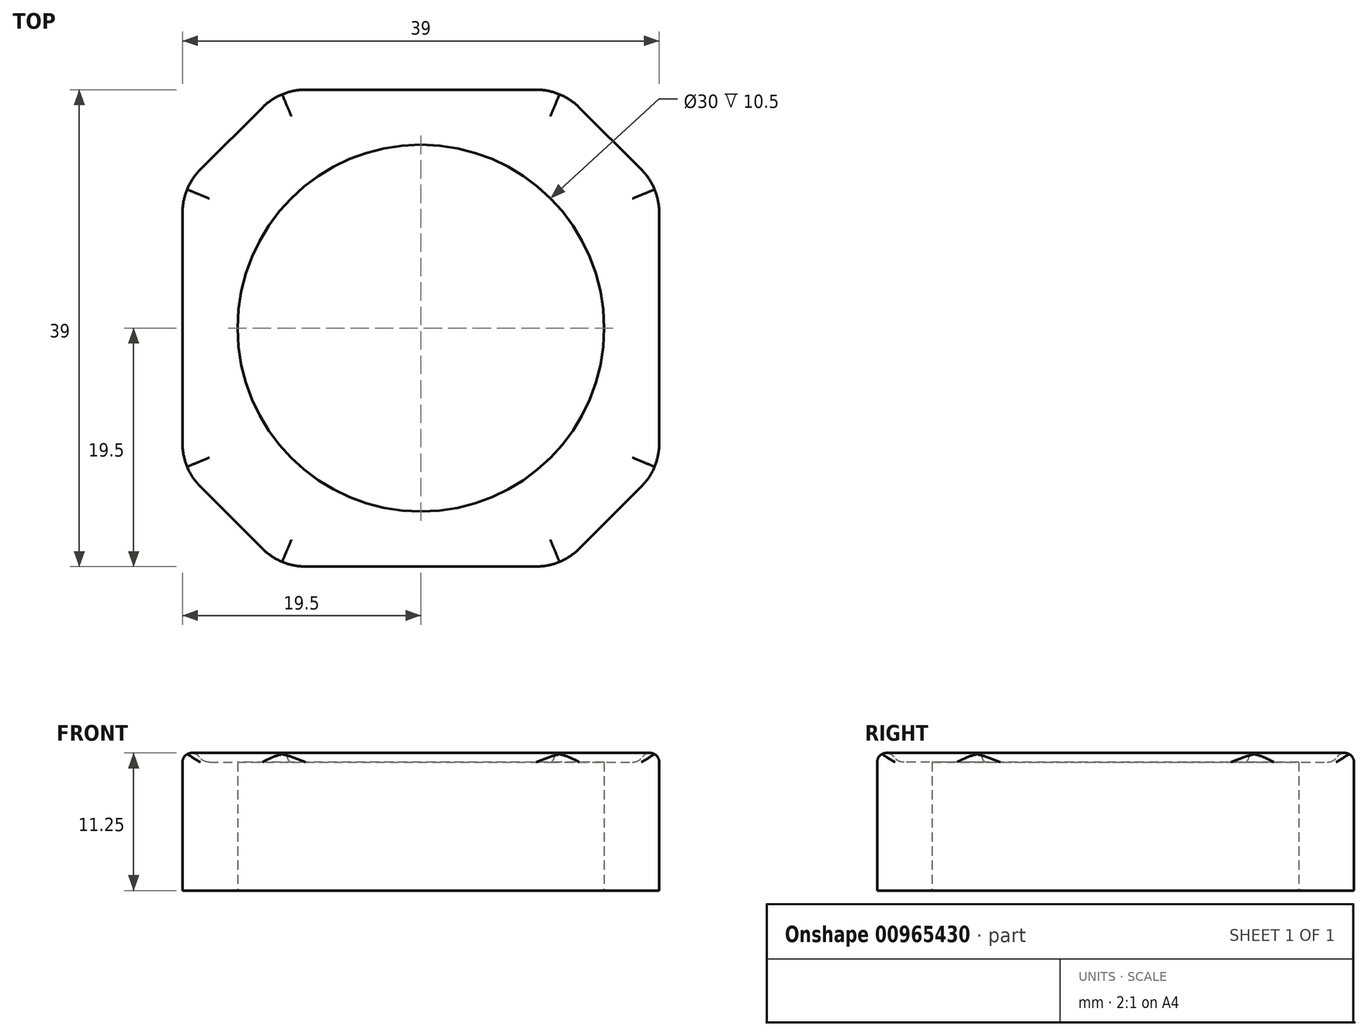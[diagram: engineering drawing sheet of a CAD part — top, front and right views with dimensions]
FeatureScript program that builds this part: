
annotation { "Feature Type Name" : "Feature", "Feature Type Description" : "" }
export const myFeature = defineFeature(function(context is Context, id is Id, definition is map)
    precondition{}
    {
        {
            var Q0;
            Q0=qCreatedBy(makeId("Top.planeOp"),FACE);
            var sketch = newSketch(context, id + "F0", { "sketchPlane" : qUnion([Q0])});
            skLineSegment(sketch, "E0.bottom", {"start": v(19.5, -19.5) * mm, "end": v(-19.5, -19.5) * mm});
            skLineSegment(sketch, "E0.top", {"start": v(19.5, 19.5) * mm, "end": v(-19.5, 19.5) * mm});
            skLineSegment(sketch, "E0.left", {"start": v(19.5, -19.5) * mm, "end": v(19.5, 19.5) * mm});
            skLineSegment(sketch, "E0.right", {"start": v(-19.5, -19.5) * mm, "end": v(-19.5, 19.5) * mm});
            skPoint(sketch, "E0.middle", {"position": v(0, 0) * mm});
            skLineSegment(sketch, "E1", {"start": v(-19.5, 11.5) * mm, "end": v(-11.5, 19.5) * mm});
            skLineSegment(sketch, "E2.MirrorCS", {"start": v(19.5, 11.5) * mm, "end": v(11.5, 19.5) * mm});
            skLineSegment(sketch, "E3.MirrorCS", {"start": v(-19.5, -11.5) * mm, "end": v(-11.5, -19.5) * mm});
            skLineSegment(sketch, "E4.MirrorCS", {"start": v(19.5, -11.5) * mm, "end": v(11.5, -19.5) * mm});
            skCircle(sketch, "E5", {"center": v(0, 0) * mm, "radius": 15 * mm});
            skSolve(sketch);
        }
        {
            var Q0;
            {var subQ0=sQuery(id+"F0.wireOp",EDGE,"E1");Q0=makeQuery(id+"F0.imprint","IMPRINT",FACE,{"disambiguationData":[TD([[makeQuery(id+"F0.imprint","IMPRINT",EDGE,{"derivedFrom":subQ0}),-1.0]])]});}
            extrude(context, id + "F1", {"entities" : qUnion([Q0]), "depth" : 10.5 * mm, "offsetDistance" : 25 * mm});
        }
        {
            var Q0;
            Q0=makeQuery(id+"F1.opExtrude","CAP_FACE",FACE,{"disambiguationData":[OSD([sQuery(id+"F0.wireOp",EDGE,"E0.bottom"),sQuery(id+"F0.wireOp",EDGE,"E0.top"),sQuery(id+"F0.wireOp",EDGE,"E0.left"),sQuery(id+"F0.wireOp",EDGE,"E0.right"),sQuery(id+"F0.wireOp",EDGE,"E1"),sQuery(id+"F0.wireOp",EDGE,"E2.MirrorCS"),sQuery(id+"F0.wireOp",EDGE,"E3.MirrorCS"),sQuery(id+"F0.wireOp",EDGE,"E4.MirrorCS"),sQuery(id+"F0.wireOp",EDGE,"E5")])],"isStart":false});
            var sketch = newSketch(context, id + "F2", { "sketchPlane" : qUnion([Q0])});
            skLineSegment(sketch, "E6.bottom", {"start": v(18.75, 18.75) * mm, "end": v(11.19, 18.75) * mm});
            skLineSegment(sketch, "E6.top", {"start": v(18.75, -18.75) * mm, "end": v(11.19, -18.75) * mm});
            skLineSegment(sketch, "E6.left", {"start": v(18.75, 18.75) * mm, "end": v(18.75, 11.19) * mm});
            skLineSegment(sketch, "E6.right", {"start": v(-18.75, 18.75) * mm, "end": v(-18.75, -18.75) * mm});
            skPoint(sketch, "E6.middle", {"position": v(0, 0) * mm});
            skLineSegment(sketch, "E7", {"start": v(-18.75, 11.19) * mm, "end": v(-18.75, 11.19) * mm});
            skLineSegment(sketch, "E8.MirrorCS", {"start": v(18.75, 11.19) * mm, "end": v(11.19, 18.75) * mm});
            skLineSegment(sketch, "E9.MirrorCS", {"start": v(-18.75, -11.19) * mm, "end": v(-11.19, -18.75) * mm});
            skLineSegment(sketch, "E10.MirrorCS", {"start": v(18.75, -11.19) * mm, "end": v(11.19, -18.75) * mm});
            skLineSegment(sketch, "E11.MirrorCS", {"start": v(-18.75, -18.75) * mm, "end": v(-11.19, -18.75) * mm});
            skLineSegment(sketch, "E12.MirrorCS", {"start": v(-18.75, 18.75) * mm, "end": v(-18.75, 11.19) * mm});
            skLineSegment(sketch, "E13", {"start": v(11.19, 18.75) * mm, "end": v(-11.19, 18.75) * mm});
            skLineSegment(sketch, "E14", {"start": v(-11.19, 18.75) * mm, "end": v(-18.75, 18.75) * mm});
            skLineSegment(sketch, "E15", {"start": v(-18.75, 11.19) * mm, "end": v(-11.19, 18.75) * mm});
            skLineSegment(sketch, "E16", {"start": v(-18.75, -11.19) * mm, "end": v(-18.75, -18.75) * mm});
            skLineSegment(sketch, "E17", {"start": v(-11.19, -18.75) * mm, "end": v(-11.19, -18.75) * mm});
            skLineSegment(sketch, "E18", {"start": v(11.19, -18.75) * mm, "end": v(18.75, -18.75) * mm});
            skLineSegment(sketch, "E19", {"start": v(18.75, -11.19) * mm, "end": v(18.75, -18.75) * mm});
            skLineSegment(sketch, "E20", {"start": v(18.75, 11.19) * mm, "end": v(18.75, -11.19) * mm});
            skLineSegment(sketch, "E21", {"start": v(-18.75, 11.19) * mm, "end": v(-18.75, -11.19) * mm});
            skLineSegment(sketch, "E22", {"start": v(-11.19, -18.75) * mm, "end": v(11.19, -18.75) * mm});
            skLineSegment(sketch, "E23", {"start": v(11.19, -18.75) * mm, "end": v(11.19, -18.75) * mm});
            skLineSegment(sketch, "E24", {"start": v(11.19, -18.75) * mm, "end": v(-11.19, -18.75) * mm});
            skLineSegment(sketch, "E25", {"start": v(-11.19, -18.75) * mm, "end": v(-18.75, -18.75) * mm});
            skSolve(sketch);
        }
        {
            var Q0;
            Q0=qCreatedBy(makeId("Front.planeOp"),FACE);
            var sketch = newSketch(context, id + "F3", { "sketchPlane" : qUnion([Q0])});
            skCircle(sketch, "E26", {"center": v(18.75, 10.5) * mm, "radius": 0.75 * mm});
            skSolve(sketch);
        }
        {
            var Q0;
            Q0=makeQuery(id+"F3.imprint","IMPRINT",FACE,{"disambiguationData":[TD([[makeQuery(id+"F3.imprint","IMPRINT",EDGE,{"derivedFrom":sQuery(id+"F3.wireOp",EDGE,"E26")}),1.0]])]});
            var Q1;
            Q1=sQuery(id+"F2.wireOp",EDGE,"E20");
            var Q2;
            Q2=sQuery(id+"F2.wireOp",EDGE,"E8.MirrorCS");
            var Q3;
            Q3=sQuery(id+"F2.wireOp",EDGE,"E13");
            var Q4;
            Q4=sQuery(id+"F2.wireOp",EDGE,"E15");
            var Q5;
            Q5=sQuery(id+"F2.wireOp",EDGE,"E10.MirrorCS");
            var Q6;
            Q6=sQuery(id+"F2.wireOp",EDGE,"E21");
            var Q7;
            Q7=sQuery(id+"F2.wireOp",EDGE,"E9.MirrorCS");
            var Q8;
            Q8=sQuery(id+"F2.wireOp",EDGE,"E22");
            sweep(context, id + "F4", {"operationType" : NewBodyOperationType.ADD, "profiles" : qUnion([Q0]), "path" : qUnion([Q1, Q2, Q3, Q4, Q5, Q6, Q7, Q8])});
        }
        {
            var Q0;
            Q0=makeQuery(id+"F4.boolean.opBoolean","INTERSECT",EDGE,{"derivedFrom":[makeQuery(id+"F1.opExtrude","CAP_FACE",FACE,{"disambiguationData":[OSD([sQuery(id+"F0.wireOp",EDGE,"E0.bottom"),sQuery(id+"F0.wireOp",EDGE,"E0.top"),sQuery(id+"F0.wireOp",EDGE,"E0.left"),sQuery(id+"F0.wireOp",EDGE,"E0.right"),sQuery(id+"F0.wireOp",EDGE,"E1"),sQuery(id+"F0.wireOp",EDGE,"E2.MirrorCS"),sQuery(id+"F0.wireOp",EDGE,"E3.MirrorCS"),sQuery(id+"F0.wireOp",EDGE,"E4.MirrorCS"),sQuery(id+"F0.wireOp",EDGE,"E5")])],"isStart":false}),makeQuery(id+"F4.opSweep","SWEPT_FACE",FACE,{"disambiguationData":[OSD([sQuery(id+"F2.wireOp",EDGE,"E21"),sQuery(id+"F3.wireOp",EDGE,"E26")])]})]});
            var Q1;
            Q1=makeQuery(id+"F4.boolean.opBoolean","INTERSECT",EDGE,{"derivedFrom":[makeQuery(id+"F1.opExtrude","CAP_FACE",FACE,{"disambiguationData":[OSD([sQuery(id+"F0.wireOp",EDGE,"E0.bottom"),sQuery(id+"F0.wireOp",EDGE,"E0.top"),sQuery(id+"F0.wireOp",EDGE,"E0.left"),sQuery(id+"F0.wireOp",EDGE,"E0.right"),sQuery(id+"F0.wireOp",EDGE,"E1"),sQuery(id+"F0.wireOp",EDGE,"E2.MirrorCS"),sQuery(id+"F0.wireOp",EDGE,"E3.MirrorCS"),sQuery(id+"F0.wireOp",EDGE,"E4.MirrorCS"),sQuery(id+"F0.wireOp",EDGE,"E5")])],"isStart":false}),makeQuery(id+"F4.opSweep","SWEPT_FACE",FACE,{"disambiguationData":[OSD([sQuery(id+"F2.wireOp",EDGE,"E9.MirrorCS"),sQuery(id+"F3.wireOp",EDGE,"E26")])]})]});
            var Q2;
            Q2=makeQuery(id+"F4.boolean.opBoolean","INTERSECT",EDGE,{"derivedFrom":[makeQuery(id+"F1.opExtrude","CAP_FACE",FACE,{"disambiguationData":[OSD([sQuery(id+"F0.wireOp",EDGE,"E0.bottom"),sQuery(id+"F0.wireOp",EDGE,"E0.top"),sQuery(id+"F0.wireOp",EDGE,"E0.left"),sQuery(id+"F0.wireOp",EDGE,"E0.right"),sQuery(id+"F0.wireOp",EDGE,"E1"),sQuery(id+"F0.wireOp",EDGE,"E2.MirrorCS"),sQuery(id+"F0.wireOp",EDGE,"E3.MirrorCS"),sQuery(id+"F0.wireOp",EDGE,"E4.MirrorCS"),sQuery(id+"F0.wireOp",EDGE,"E5")])],"isStart":false}),makeQuery(id+"F4.opSweep","SWEPT_FACE",FACE,{"disambiguationData":[OSD([sQuery(id+"F2.wireOp",EDGE,"E15"),sQuery(id+"F3.wireOp",EDGE,"E26")])]})]});
            var Q3;
            Q3=makeQuery(id+"F4.boolean.opBoolean","INTERSECT",EDGE,{"derivedFrom":[makeQuery(id+"F1.opExtrude","CAP_FACE",FACE,{"disambiguationData":[OSD([sQuery(id+"F0.wireOp",EDGE,"E0.bottom"),sQuery(id+"F0.wireOp",EDGE,"E0.top"),sQuery(id+"F0.wireOp",EDGE,"E0.left"),sQuery(id+"F0.wireOp",EDGE,"E0.right"),sQuery(id+"F0.wireOp",EDGE,"E1"),sQuery(id+"F0.wireOp",EDGE,"E2.MirrorCS"),sQuery(id+"F0.wireOp",EDGE,"E3.MirrorCS"),sQuery(id+"F0.wireOp",EDGE,"E4.MirrorCS"),sQuery(id+"F0.wireOp",EDGE,"E5")])],"isStart":false}),makeQuery(id+"F4.opSweep","SWEPT_FACE",FACE,{"disambiguationData":[OSD([sQuery(id+"F2.wireOp",EDGE,"E13"),sQuery(id+"F3.wireOp",EDGE,"E26")])]})]});
            var Q4;
            Q4=makeQuery(id+"F4.boolean.opBoolean","INTERSECT",EDGE,{"derivedFrom":[makeQuery(id+"F1.opExtrude","CAP_FACE",FACE,{"disambiguationData":[OSD([sQuery(id+"F0.wireOp",EDGE,"E0.bottom"),sQuery(id+"F0.wireOp",EDGE,"E0.top"),sQuery(id+"F0.wireOp",EDGE,"E0.left"),sQuery(id+"F0.wireOp",EDGE,"E0.right"),sQuery(id+"F0.wireOp",EDGE,"E1"),sQuery(id+"F0.wireOp",EDGE,"E2.MirrorCS"),sQuery(id+"F0.wireOp",EDGE,"E3.MirrorCS"),sQuery(id+"F0.wireOp",EDGE,"E4.MirrorCS"),sQuery(id+"F0.wireOp",EDGE,"E5")])],"isStart":false}),makeQuery(id+"F4.opSweep","SWEPT_FACE",FACE,{"disambiguationData":[OSD([sQuery(id+"F2.wireOp",EDGE,"E8.MirrorCS"),sQuery(id+"F3.wireOp",EDGE,"E26")])]})]});
            var Q5;
            Q5=makeQuery(id+"F4.boolean.opBoolean","INTERSECT",EDGE,{"derivedFrom":[makeQuery(id+"F1.opExtrude","CAP_FACE",FACE,{"disambiguationData":[OSD([sQuery(id+"F0.wireOp",EDGE,"E0.bottom"),sQuery(id+"F0.wireOp",EDGE,"E0.top"),sQuery(id+"F0.wireOp",EDGE,"E0.left"),sQuery(id+"F0.wireOp",EDGE,"E0.right"),sQuery(id+"F0.wireOp",EDGE,"E1"),sQuery(id+"F0.wireOp",EDGE,"E2.MirrorCS"),sQuery(id+"F0.wireOp",EDGE,"E3.MirrorCS"),sQuery(id+"F0.wireOp",EDGE,"E4.MirrorCS"),sQuery(id+"F0.wireOp",EDGE,"E5")])],"isStart":false}),makeQuery(id+"F4.opSweep","SWEPT_FACE",FACE,{"disambiguationData":[OSD([sQuery(id+"F2.wireOp",EDGE,"E20"),sQuery(id+"F3.wireOp",EDGE,"E26")])]})]});
            var Q6;
            Q6=makeQuery(id+"F4.boolean.opBoolean","INTERSECT",EDGE,{"derivedFrom":[makeQuery(id+"F1.opExtrude","CAP_FACE",FACE,{"disambiguationData":[OSD([sQuery(id+"F0.wireOp",EDGE,"E0.bottom"),sQuery(id+"F0.wireOp",EDGE,"E0.top"),sQuery(id+"F0.wireOp",EDGE,"E0.left"),sQuery(id+"F0.wireOp",EDGE,"E0.right"),sQuery(id+"F0.wireOp",EDGE,"E1"),sQuery(id+"F0.wireOp",EDGE,"E2.MirrorCS"),sQuery(id+"F0.wireOp",EDGE,"E3.MirrorCS"),sQuery(id+"F0.wireOp",EDGE,"E4.MirrorCS"),sQuery(id+"F0.wireOp",EDGE,"E5")])],"isStart":false}),makeQuery(id+"F4.opSweep","SWEPT_FACE",FACE,{"disambiguationData":[OSD([sQuery(id+"F2.wireOp",EDGE,"E10.MirrorCS"),sQuery(id+"F3.wireOp",EDGE,"E26")])]})]});
            var Q7;
            Q7=makeQuery(id+"F4.boolean.opBoolean","INTERSECT",EDGE,{"derivedFrom":[makeQuery(id+"F1.opExtrude","CAP_FACE",FACE,{"disambiguationData":[OSD([sQuery(id+"F0.wireOp",EDGE,"E0.bottom"),sQuery(id+"F0.wireOp",EDGE,"E0.top"),sQuery(id+"F0.wireOp",EDGE,"E0.left"),sQuery(id+"F0.wireOp",EDGE,"E0.right"),sQuery(id+"F0.wireOp",EDGE,"E1"),sQuery(id+"F0.wireOp",EDGE,"E2.MirrorCS"),sQuery(id+"F0.wireOp",EDGE,"E3.MirrorCS"),sQuery(id+"F0.wireOp",EDGE,"E4.MirrorCS"),sQuery(id+"F0.wireOp",EDGE,"E5")])],"isStart":false}),makeQuery(id+"F4.opSweep","SWEPT_FACE",FACE,{"disambiguationData":[OSD([sQuery(id+"F2.wireOp",EDGE,"E22"),sQuery(id+"F3.wireOp",EDGE,"E26")])]})]});
            fillet(context, id + "F5", {"entities" : qUnion([Q0, Q1, Q2, Q3, Q4, Q5, Q6, Q7]), "radius" : 1 * mm, "tangentPropagation" : true, "allowEdgeOverflow" : false});
        }
        {
            var Q0;
            Q0=makeQuery(id+"F1.opExtrude","SWEPT_EDGE",EDGE,{"disambiguationData":[OSD([sQuery(id+"F0.wireOp",EDGE,"E0.right"),sQuery(id+"F0.wireOp",EDGE,"E3.MirrorCS")])]});
            var Q1;
            Q1=makeQuery(id+"F1.opExtrude","SWEPT_EDGE",EDGE,{"disambiguationData":[OSD([sQuery(id+"F0.wireOp",EDGE,"E0.bottom"),sQuery(id+"F0.wireOp",EDGE,"E3.MirrorCS")])]});
            var Q2;
            Q2=makeQuery(id+"F1.opExtrude","SWEPT_EDGE",EDGE,{"disambiguationData":[OSD([sQuery(id+"F0.wireOp",EDGE,"E0.bottom"),sQuery(id+"F0.wireOp",EDGE,"E4.MirrorCS")])]});
            var Q3;
            Q3=makeQuery(id+"F1.opExtrude","SWEPT_EDGE",EDGE,{"disambiguationData":[OSD([sQuery(id+"F0.wireOp",EDGE,"E0.left"),sQuery(id+"F0.wireOp",EDGE,"E4.MirrorCS")])]});
            var Q4;
            Q4=makeQuery(id+"F1.opExtrude","SWEPT_EDGE",EDGE,{"disambiguationData":[OSD([sQuery(id+"F0.wireOp",EDGE,"E0.top"),sQuery(id+"F0.wireOp",EDGE,"E1")])]});
            var Q5;
            Q5=makeQuery(id+"F1.opExtrude","SWEPT_EDGE",EDGE,{"disambiguationData":[OSD([sQuery(id+"F0.wireOp",EDGE,"E0.right"),sQuery(id+"F0.wireOp",EDGE,"E1")])]});
            var Q6;
            Q6=makeQuery(id+"F1.opExtrude","SWEPT_EDGE",EDGE,{"disambiguationData":[OSD([sQuery(id+"F0.wireOp",EDGE,"E0.top"),sQuery(id+"F0.wireOp",EDGE,"E2.MirrorCS")])]});
            var Q7;
            Q7=makeQuery(id+"F1.opExtrude","SWEPT_EDGE",EDGE,{"disambiguationData":[OSD([sQuery(id+"F0.wireOp",EDGE,"E0.left"),sQuery(id+"F0.wireOp",EDGE,"E2.MirrorCS")])]});
            fillet(context, id + "F6", {"entities" : qUnion([Q0, Q1, Q2, Q3, Q4, Q5, Q6, Q7]), "radius" : 5 * mm, "allowEdgeOverflow" : false});
        }
    });
